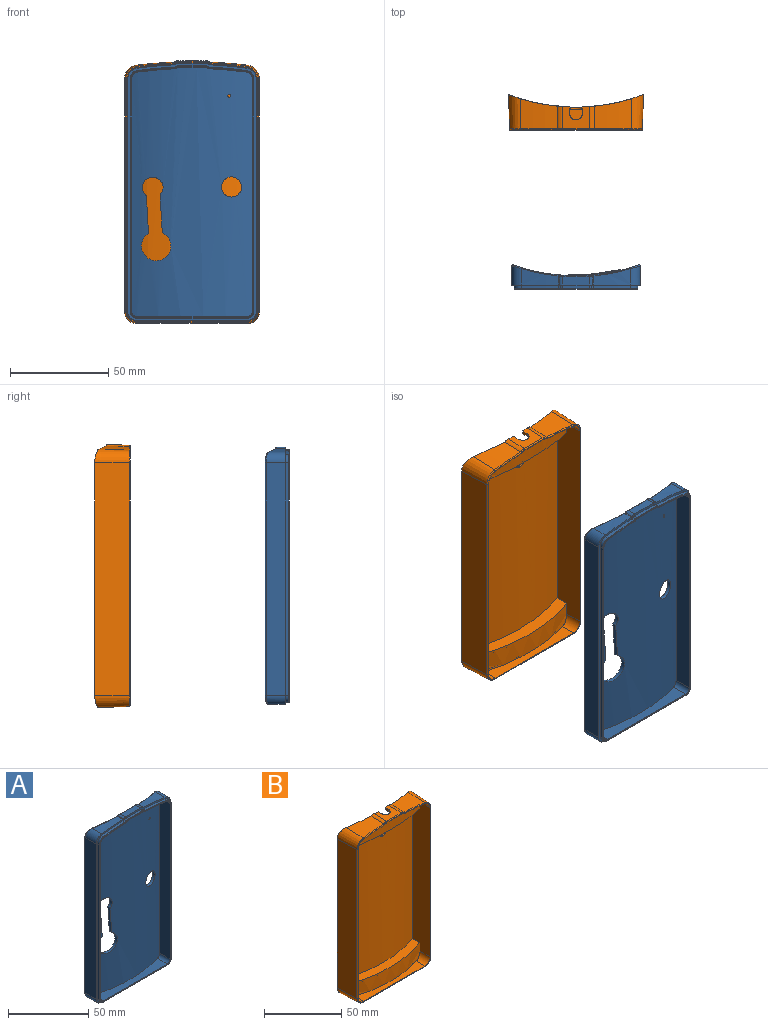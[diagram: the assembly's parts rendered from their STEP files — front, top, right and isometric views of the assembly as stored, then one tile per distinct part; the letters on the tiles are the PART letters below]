
ASSEMBLY  parts=2 mates=1
PART A: 121 faces, bbox 76.7x16.8x131.1 mm
  f0: cylinder r=98.14mm len=127mm, axis (0,0,-1), area 7374mm2, adj f1,f102,f103,f104,f105,f106,f107,f108
  f1: cylinder r=0.75mm len=2.04mm, axis (0,1,0), area 9.6mm2, adj f0,f2
  f2: cylinder r=96.14mm len=52.21mm, axis (0,0,-1), area 301mm2, adj f1,f3,f95,f96,f97,f98,f99,f100
  f3: cylinder r=2.75mm len=3.8mm, axis (0,1,0), area 0.1mm2, adj f2,f4,f95
  f4: bspline ~5.13x3.42mm, area 4.4mm2, adj f3,f5,f6,f101
  f5: bspline ~7.44x3.43mm, area 6.1mm2, adj f4,f6,f95,f96
  f6: cylinder r=96.14mm len=11.74mm, axis (0,0,-1), area 0mm2, adj f4,f5,f7,f94
  f7: bspline ~15.6x6.8mm, area 7.1mm2, adj f6,f8,f21,f94,f96
  f8: bspline ~38.52x16.14mm, area 31mm2, adj f7,f9,f11,f20
  f9: plane 38.46x15.89mm, normal (-0.92,0,0.38), area 1.5mm2, adj f8,f10,f21
  f10: cylinder r=3.75mm len=3.1mm, axis (0,1,0), area 0.2mm2, adj f9,f20,f21
  f11: cylinder r=96.14mm len=53.2mm, axis (0,0,-1), area 1.3mm2, adj f8,f12,f13,f14,f17,f18,f19,f20
  f12: bspline ~5.6x5.03mm, area 5.7mm2, adj f11,f13,f20,f21
  f13: bspline ~55.44x23.19mm, area 39.4mm2, adj f11,f12,f14,f21
  f14: bspline ~4.17x2.87mm, area 3.1mm2, adj f11,f13,f15,f21,f101
  f15: bspline ~1.05x0.54mm, area 0.2mm2, adj f14,f16,f94,f101
  f16: cylinder r=3.75mm len=0.22mm, axis (0,1,0), area 0mm2, adj f15,f21
  f17: bspline ~3.24x2.35mm, area 2.5mm2, adj f11,f18,f100,f101
  f18: bspline ~46.9x19.56mm, area 36.7mm2, adj f11,f17,f19,f99
  f19: bspline ~4.92x3.53mm, area 3.9mm2, adj f11,f18,f97,f98
  f20: bspline ~3.72x2.62mm, area 2.9mm2, adj f8,f10,f11,f12
  f21: cylinder r=96.14mm len=130mm, axis (0,0,-1), area 7498.8mm2, adj f7,f9,f10,f12,f13,f14,f16,f22
  f22: bspline ~3.13x1.42mm, area 1.5mm2, adj f21,f23,f81,f93
  f23: cylinder r=3.17mm len=4.61mm, axis (0,1,0), area 9.1mm2, adj f22,f24,f79,f80
  f24: plane 131x65.5mm, normal (0,-1,0), area 451.5mm2, adj f23,f25,f26,f27,f28,f29,f30,f31
  f25: cylinder r=206.86mm len=18.83mm, axis (0,1,0), area 123.5mm2, adj f24,f26,f80,f82
  f26: cylinder r=5.5mm len=9.79mm, axis (0,1,0), area 71.7mm2, adj f24,f25,f27,f83
  f27: plane 118.55x9.79mm, normal (1,0,0), area 1160.6mm2, adj f24,f26,f28,f84
  f28: cylinder r=4.5mm len=9.79mm, axis (0,1,0), area 64.5mm2, adj f24,f27,f29,f85
  f29: plane 56.5x8.47mm, normal (0,0,-1), area 318.9mm2, adj f24,f28,f30,f86
  f30: cylinder r=4.5mm len=9.79mm, axis (0,1,0), area 64.5mm2, adj f24,f29,f31,f87
  f31: plane 118.55x9.79mm, normal (-1,0,0), area 1160.6mm2, adj f24,f30,f32,f88
  f32: cylinder r=5.5mm len=9.79mm, axis (0,1,0), area 71.7mm2, adj f24,f31,f33,f89
  f33: cylinder r=206.86mm len=18.83mm, axis (0,1,0), area 123.5mm2, adj f24,f32,f34,f90
  f34: cylinder r=1mm len=4.68mm, axis (0,1,0), area 2.7mm2, adj f24,f33,f35,f91
  f35: cylinder r=3.17mm len=4.61mm, axis (0,1,0), area 9.1mm2, adj f24,f34,f79,f92
  f36: plane 56.5x1.8mm, normal (0,0,-1), area 101.7mm2, adj f24,f37,f66,f78
  f37: cylinder r=0.2mm len=56.5mm, axis (1,0,0), area 17.7mm2, adj f36,f38,f64,f65
  f38: plane 128.2x62.7mm, normal (0,-1,0), area 148mm2, adj f37,f39,f40,f41,f42,f43,f44,f45
  f39: torus R=2.8mm, axis (0,-1,0), area 0.5mm2, adj f38,f40,f52,f114
  f40: torus R=1.37mm, axis (0,-1,0), area 0.2mm2, adj f38,f39,f41,f113
  f41: cylinder r=0.2mm len=13.5mm, axis (-1,0,0), area 4.2mm2, adj f38,f40,f42,f112
  f42: torus R=1.37mm, axis (0,-1,0), area 0.2mm2, adj f38,f41,f43,f111
  f43: torus R=2.8mm, axis (0,-1,0), area 0.5mm2, adj f38,f42,f44,f110
  f44: torus R=205.06mm, axis (0,-1,0), area 5.9mm2, adj f38,f43,f45,f109
  f45: torus R=3.7mm, axis (0,-1,0), area 1.6mm2, adj f38,f44,f46,f108
  f46: cylinder r=0.2mm len=118.55mm, axis (0,0,-1), area 37.2mm2, adj f38,f45,f47,f107
  f47: torus R=2.7mm, axis (0,-1,0), area 1.3mm2, adj f38,f46,f48,f120
  f48: cylinder r=0.2mm len=56.5mm, axis (1,0,0), area 17.7mm2, adj f38,f47,f49,f119
  f49: torus R=2.7mm, axis (0,-1,0), area 1.3mm2, adj f38,f48,f50,f118
  f50: cylinder r=0.2mm len=118.55mm, axis (0,0,1), area 37.2mm2, adj f38,f49,f51,f117
  f51: torus R=3.7mm, axis (0,-1,0), area 1.6mm2, adj f38,f50,f52,f116
  f52: torus R=205.06mm, axis (0,-1,0), area 5.9mm2, adj f38,f39,f51,f115
  f53: cylinder r=0.2mm len=118.55mm, axis (0,0,-1), area 37.2mm2, adj f38,f54,f65,f77
  f54: torus R=4.1mm, axis (0,-1,0), area 1.9mm2, adj f38,f53,f55,f76
  f55: torus R=205.46mm, axis (0,-1,0), area 5.9mm2, adj f38,f54,f56,f75
  f56: torus R=2.4mm, axis (0,-1,0), area 0.4mm2, adj f38,f55,f57,f74
  f57: torus R=1.77mm, axis (0,-1,0), area 0.4mm2, adj f38,f56,f58,f73
  f58: cylinder r=0.2mm len=13.5mm, axis (-1,0,0), area 4.2mm2, adj f38,f57,f59,f72
  f59: torus R=1.77mm, axis (0,-1,0), area 0.4mm2, adj f38,f58,f60,f71
  f60: torus R=2.4mm, axis (0,-1,0), area 0.4mm2, adj f38,f59,f61,f70
  f61: torus R=205.46mm, axis (0,-1,0), area 5.9mm2, adj f38,f60,f62,f69
  f62: torus R=4.1mm, axis (0,-1,0), area 1.9mm2, adj f38,f61,f63,f68
  f63: cylinder r=0.2mm len=118.55mm, axis (0,0,1), area 37.2mm2, adj f38,f62,f64,f67
  f64: torus R=3.1mm, axis (0,-1,0), area 1.6mm2, adj f37,f38,f63,f66
  f65: torus R=3.1mm, axis (0,-1,0), area 1.6mm2, adj f37,f38,f53,f78
  f66: cylinder r=3.3mm len=3.3mm, axis (0,-1,0), area 9.3mm2, adj f24,f36,f64,f67
  f67: plane 118.55x1.8mm, normal (1,0,0), area 213.4mm2, adj f24,f63,f66,f68
  f68: cylinder r=4.3mm len=4.26mm, axis (0,-1,0), area 11.1mm2, adj f24,f62,f67,f69
  f69: cylinder r=205.66mm len=18.72mm, axis (0,-1,0), area 33.9mm2, adj f24,f61,f68,f70
  f70: cylinder r=2.2mm len=1.8mm, axis (0,-1,0), area 2.3mm2, adj f24,f60,f69,f71
  f71: cylinder r=1.97mm len=1.8mm, axis (0,-1,0), area 2.2mm2, adj f24,f59,f70,f72
  f72: plane 13.5x1.8mm, normal (0,0,1), area 24.3mm2, adj f24,f58,f71,f73
  f73: cylinder r=1.97mm len=1.8mm, axis (0,-1,0), area 2.2mm2, adj f24,f57,f72,f74
  f74: cylinder r=2.2mm len=1.8mm, axis (0,-1,0), area 2.3mm2, adj f24,f56,f73,f75
  f75: cylinder r=205.66mm len=18.72mm, axis (0,-1,0), area 33.9mm2, adj f24,f55,f74,f76
  f76: cylinder r=4.3mm len=4.26mm, axis (0,-1,0), area 11.1mm2, adj f24,f54,f75,f77
  f77: plane 118.55x1.8mm, normal (-1,0,0), area 213.4mm2, adj f24,f53,f76,f78
  f78: cylinder r=3.3mm len=3.3mm, axis (0,-1,0), area 9.3mm2, adj f24,f36,f65,f77
  f79: plane 13.5x4.49mm, normal (0,0,1), area 58.4mm2, adj f23,f24,f35,f93
  f80: cylinder r=1mm len=4.68mm, axis (0,1,0), area 2.7mm2, adj f23,f24,f25,f81
  f81: bspline ~1.4x0.87mm, area 0.6mm2, adj f21,f22,f80,f82
  f82: bspline ~39.25x8.35mm, area 15.3mm2, adj f21,f25,f81,f83
  f83: bspline ~6.74x6.16mm, area 7mm2, adj f21,f26,f82,f84
  f84: cylinder r=0.5mm len=118.55mm, axis (0,0,-1), area 113.3mm2, adj f21,f27,f83,f85
  f85: bspline ~5.66x5.52mm, area 6.2mm2, adj f21,f28,f84,f86
  f86: torus R=96.64mm, axis (0,0,1), area 44.9mm2, adj f21,f29,f85,f87
  f87: bspline ~5.66x5.52mm, area 6.2mm2, adj f21,f30,f86,f88
  f88: cylinder r=0.5mm len=118.55mm, axis (0,0,-1), area 113.3mm2, adj f21,f31,f87,f89
  f89: bspline ~6.16x5.82mm, area 7mm2, adj f21,f32,f88,f90
  f90: bspline ~39.25x8.35mm, area 15.3mm2, adj f21,f33,f89,f91
  f91: bspline ~1.19x0.87mm, area 0.6mm2, adj f21,f34,f90,f92
  f92: bspline ~2.75x1.1mm, area 1.5mm2, adj f21,f35,f91,f93
  f93: torus R=96.64mm, axis (0,0,1), area 10.6mm2, adj f21,f22,f79,f92
  f94: bspline ~5.18x3.75mm, area 5.5mm2, adj f6,f7,f15,f21,f101
  f95: plane 7.25x2.98mm, normal (0.92,0,-0.38), area 0.1mm2, adj f2,f3,f5
  f96: bspline ~39.65x16.69mm, area 33.4mm2, adj f2,f5,f7,f11,f97
  f97: bspline ~3.36x2.2mm, area 2.9mm2, adj f2,f11,f19,f96
  f98: cylinder r=2.75mm len=3.78mm, axis (0,1,0), area 0.4mm2, adj f2,f19,f99
  f99: plane 46.71x19.21mm, normal (-0.92,0,0.38), area 2.7mm2, adj f2,f18,f98,f100
  f100: cylinder r=2.75mm len=2.35mm, axis (0,1,0), area 0mm2, adj f2,f17,f99
  f101: bspline ~1.39x0.56mm, area 0.2mm2, adj f2,f4,f14,f15,f17,f94
  f102: cylinder r=5.12mm len=10.25mm, axis (0,1,0), area 65.9mm2, adj f0,f21
  f103: cylinder r=7.5mm len=15mm, axis (0,1,0), area 81.3mm2, adj f0,f21,f104,f106
  f104: plane 19.33x2.22mm, normal (-1,0,-0.06), area 39.2mm2, adj f0,f21,f103,f105
  f105: cylinder r=5.25mm len=10.5mm, axis (0,1,0), area 51.8mm2, adj f0,f21,f104,f106
  f106: plane 19.34x2.34mm, normal (1,0,0.06), area 39.8mm2, adj f0,f21,f103,f105
  f107: plane 118.55x9.49mm, normal (1,0,0), area 1125.3mm2, adj f0,f46,f108,f120
  f108: cylinder r=3.5mm len=9.49mm, axis (0,1,0), area 45.3mm2, adj f0,f45,f107,f109
  f109: cylinder r=204.86mm len=18.65mm, axis (0,1,0), area 126.6mm2, adj f0,f44,f108,f110
  f110: cylinder r=3mm len=4.97mm, axis (0,1,0), area 8.6mm2, adj f0,f43,f109,f111
  f111: cylinder r=1.17mm len=4.83mm, axis (0,1,0), area 3.5mm2, adj f0,f42,f110,f112
  f112: plane 13.5x4.78mm, normal (0,0,-1), area 62.5mm2, adj f0,f41,f111,f113
  f113: cylinder r=1.17mm len=4.83mm, axis (0,1,0), area 3.5mm2, adj f0,f40,f112,f114
  f114: cylinder r=3mm len=4.97mm, axis (0,1,0), area 8.6mm2, adj f0,f39,f113,f115
  f115: cylinder r=204.86mm len=18.65mm, axis (0,1,0), area 126.6mm2, adj f0,f52,f114,f116
  f116: cylinder r=3.5mm len=9.49mm, axis (0,1,0), area 45.3mm2, adj f0,f51,f115,f117
  f117: plane 118.55x9.49mm, normal (-1,0,0), area 1125.3mm2, adj f0,f50,f116,f118
  f118: cylinder r=2.5mm len=9.49mm, axis (0,1,0), area 35.7mm2, adj f0,f49,f117,f119
  f119: plane 56.5x8.7mm, normal (0,0,1), area 334.6mm2, adj f0,f48,f118,f120
  f120: cylinder r=2.5mm len=9.49mm, axis (0,1,0), area 35.7mm2, adj f0,f47,f107,f119
PART B: 70 faces, bbox 68.8x18x134.1 mm
  f0: cylinder r=96.1mm len=133.97mm, axis (0,0,1), area 7949.2mm2, adj f1,f2,f4,f5,f6,f7,f8,f9
  f1: plane 13.5x11.4mm, normal (0,-0.03,1), area 113.9mm2, adj f0,f4,f14,f54,f55,f56,f64
  f2: plane 13.52x7.53mm, normal (0,0.03,-1), area 60.4mm2, adj f0,f38,f39,f47,f54,f55,f56
  f3: cylinder r=96.14mm len=66mm, axis (0,0,-1), area 700.1mm2, adj f17,f18,f19,f20,f21,f22,f25,f26
  f4: cone r=4.17mm half-angle=2deg, axis (0,1,0), area 31.1mm2, adj f0,f1,f5,f66
  f5: cone r=207.86mm half-angle=2deg, axis (0,1,0), area 249.9mm2, adj f0,f4,f6,f68
  f6: cone r=6.5mm half-angle=2deg, axis (0,1,0), area 163.5mm2, adj f0,f5,f7,f67
  f7: plane 118.55x17.52mm, normal (-1,-0.03,0), area 2078mm2, adj f0,f6,f8,f65
  f8: cone r=5.5mm half-angle=2deg, axis (0,1,0), area 152.6mm2, adj f0,f7,f9,f63
  f9: plane 56.5x15.4mm, normal (0,-0.03,-1), area 710.1mm2, adj f0,f8,f10,f61
  f10: cone r=5.5mm half-angle=2deg, axis (0,1,0), area 152.6mm2, adj f0,f9,f11,f59
  f11: plane 118.55x17.52mm, normal (1,-0.03,0), area 2078mm2, adj f0,f10,f12,f57
  f12: cone r=6.5mm half-angle=2deg, axis (0,1,0), area 163.5mm2, adj f0,f11,f13,f58
  f13: cone r=207.86mm half-angle=2deg, axis (0,1,0), area 249.9mm2, adj f0,f12,f14,f60
  f14: cone r=4.17mm half-angle=2deg, axis (0,1,0), area 31.1mm2, adj f0,f1,f13,f62
  f15: plane 132.03x66.53mm, normal (0,-1,0), area 102.2mm2, adj f17,f18,f19,f20,f21,f22,f23,f24
  f16: cylinder r=96.14mm len=66mm, axis (0,0,-1), area 747.6mm2, adj f23,f24,f25,f27,f28,f50
  f17: cylinder r=5.75mm len=9.55mm, axis (0,-1,0), area 73.7mm2, adj f3,f15,f18,f25
  f18: cylinder r=207.11mm len=19.09mm, axis (0,-1,0), area 109.1mm2, adj f3,f15,f17,f19
  f19: cylinder r=3.42mm len=4.15mm, axis (0,-1,0), area 9.6mm2, adj f3,f15,f18,f26
  f20: cylinder r=3.42mm len=4.17mm, axis (0,-1,0), area 9.7mm2, adj f3,f15,f21,f26
  f21: cylinder r=207.11mm len=19.09mm, axis (0,-1,0), area 109.8mm2, adj f3,f15,f20,f22
  f22: cylinder r=5.75mm len=9.62mm, axis (0,-1,0), area 74.3mm2, adj f3,f15,f21,f27
  f23: cylinder r=4.75mm len=9.62mm, axis (0,-1,0), area 67.3mm2, adj f15,f16,f27,f28
  f24: cylinder r=4.75mm len=9.55mm, axis (0,-1,0), area 66.8mm2, adj f15,f16,f25,f28
  f25: plane 118.55x16.48mm, normal (-1,0,0), area 1872mm2, adj f3,f15,f16,f17,f24,f48,f49,f50
  f26: plane 13.5x3.99mm, normal (0,0,-1), area 51.6mm2, adj f3,f15,f19,f20
  f27: plane 118.55x16.48mm, normal (1,0,0), area 1872.8mm2, adj f3,f15,f16,f22,f23,f48,f49,f50
  f28: plane 56.5x8.02mm, normal (0,0,1), area 290.8mm2, adj f15,f16,f23,f24
  f29: plane 65.42x13.01mm, normal (0,0.03,-1), area 474.3mm2, adj f0,f30,f34,f35
  f30: plane 7.37x5.46mm, normal (1,0.03,0), area 39.3mm2, adj f0,f29,f31,f35
  f31: cone r=4.5mm half-angle=2deg, axis (0,1,0), area 49.7mm2, adj f0,f30,f32,f35
  f32: plane 56.5x11.52mm, normal (0,0.03,1), area 411.3mm2, adj f0,f31,f33,f35
  f33: cone r=4.5mm half-angle=2deg, axis (0,1,0), area 49.7mm2, adj f0,f32,f34,f35
  f34: plane 7.37x5.46mm, normal (-1,0.03,0), area 39.3mm2, adj f0,f29,f33,f35
  f35: cylinder r=96.14mm len=64.91mm, axis (0,0,1), area 597.4mm2, adj f29,f30,f31,f32,f33,f34
  f36: cone r=206.86mm half-angle=2deg, axis (0,1,0), area 137.6mm2, adj f0,f37,f46,f47
  f37: cone r=1mm half-angle=2deg, axis (0,-1,0), area 5.8mm2, adj f0,f36,f38,f47
  f38: cone r=3.17mm half-angle=2deg, axis (0,1,0), area 12.9mm2, adj f0,f2,f37,f47
  f39: cone r=3.17mm half-angle=2deg, axis (0,1,0), area 12.9mm2, adj f0,f2,f40,f47
  f40: cone r=1mm half-angle=2deg, axis (0,-1,0), area 5.8mm2, adj f0,f39,f41,f47
  f41: cone r=206.86mm half-angle=2deg, axis (0,1,0), area 137.6mm2, adj f0,f40,f42,f47
  f42: cone r=5.5mm half-angle=2deg, axis (0,1,0), area 56mm2, adj f0,f41,f43,f47
  f43: plane 7.37x4.83mm, normal (1,0.03,0), area 34.5mm2, adj f0,f42,f44,f47
  f44: cone r=216mm half-angle=2deg, axis (0,-1,0), area 438.3mm2, adj f0,f43,f45,f47,f51,f52,f53
  f45: plane 7.37x5.27mm, normal (-1,0.03,0), area 37.8mm2, adj f0,f44,f46,f47
  f46: cone r=5.5mm half-angle=2deg, axis (0,1,0), area 56mm2, adj f0,f36,f45,f47
  f47: cylinder r=96.14mm len=64.91mm, axis (0,0,1), area 601.3mm2, adj f2,f36,f37,f38,f39,f40,f41,f42
  f48: cylinder r=96.1mm len=109.2mm, axis (0,0,-1), area 7251.9mm2, adj f25,f27,f49,f50,f51,f53,f69
  f49: cylinder r=216mm len=66mm, axis (0,-1,0), area 425.6mm2, adj f3,f25,f27,f48,f51,f52,f53
  f50: plane 66x12.74mm, normal (0,0,1), area 455.1mm2, adj f16,f25,f27,f48
  f51: plane 5.56x3.31mm, normal (-1,0,0), area 6.7mm2, adj f0,f44,f48,f49,f52,f69
  f52: cylinder r=3.25mm len=6.5mm, axis (0,0,1), area 6.8mm2, adj f44,f49,f51,f53
  f53: plane 5.6x3.31mm, normal (1,0,0), area 6.8mm2, adj f0,f44,f48,f49,f52,f69
  f54: plane 3.31x1.76mm, normal (1,0,0), area 5.4mm2, adj f0,f1,f2,f55
  f55: cylinder r=3.25mm len=6.5mm, axis (0,0,1), area 16.8mm2, adj f1,f2,f54,f56
  f56: plane 3.31x1.76mm, normal (-1,0,0), area 5.4mm2, adj f0,f1,f2,f55
  f57: cylinder r=0.5mm len=118.55mm, axis (0,0,1), area 91mm2, adj f11,f15,f58,f59
  f58: torus R=6.02mm, axis (0,-1,0), area 7mm2, adj f12,f15,f57,f60
  f59: torus R=5.02mm, axis (0,-1,0), area 6.4mm2, adj f10,f15,f57,f61
  f60: torus R=207.38mm, axis (0,-1,0), area 14.6mm2, adj f13,f15,f58,f62
  f61: cylinder r=0.5mm len=56.5mm, axis (1,0,0), area 43.4mm2, adj f9,f15,f59,f63
  f62: torus R=3.68mm, axis (0,-1,0), area 2mm2, adj f14,f15,f60,f64
  f63: torus R=5.02mm, axis (0,-1,0), area 6.4mm2, adj f8,f15,f61,f65
  f64: cylinder r=0.5mm len=13.5mm, axis (-1,0,0), area 10.4mm2, adj f1,f15,f62,f66
  f65: cylinder r=0.5mm len=118.55mm, axis (0,0,-1), area 91mm2, adj f7,f15,f63,f67
  f66: torus R=3.68mm, axis (0,-1,0), area 2mm2, adj f4,f15,f64,f68
  f67: torus R=6.02mm, axis (0,-1,0), area 7mm2, adj f6,f15,f65,f68
  f68: torus R=207.38mm, axis (0,-1,0), area 14.6mm2, adj f5,f15,f66,f67
  f69: cylinder r=3.25mm len=6.5mm, axis (0,-1,0), area 10.2mm2, adj f0,f48,f51,f53
PLACE A t=(35.28,-27.93,-73.6)mm
PLACE B t=(35.28,49.1,-73.6)mm
MATE slider A.f30 <-> B.f8  axis (0,-1,0) through (39.78,-38.43,-69.1)mm
